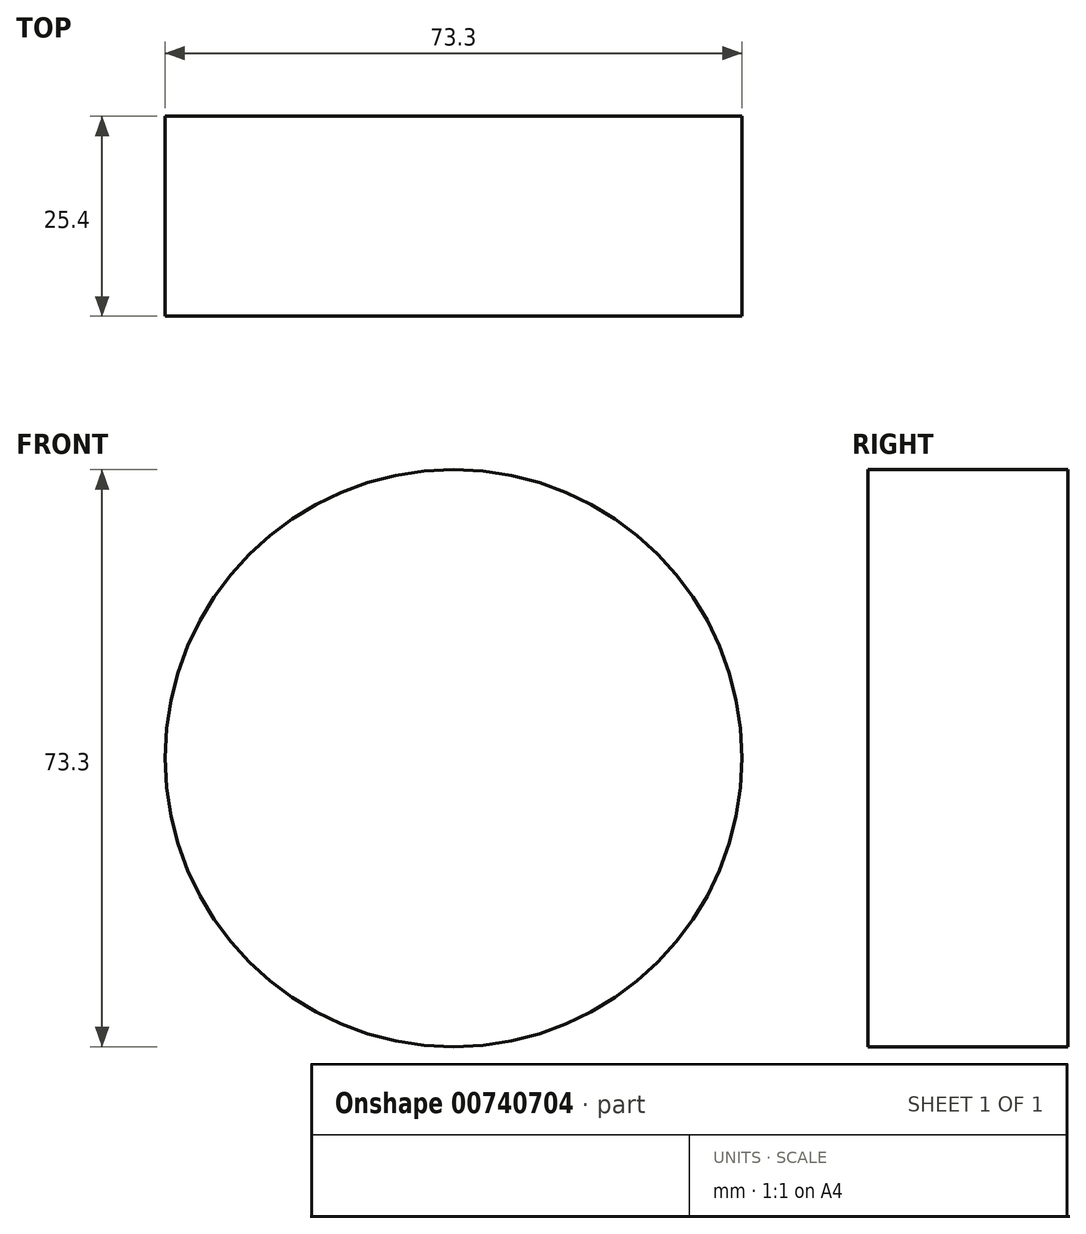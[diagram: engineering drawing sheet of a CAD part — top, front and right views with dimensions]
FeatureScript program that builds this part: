
annotation { "Feature Type Name" : "Feature", "Feature Type Description" : "" }
export const myFeature = defineFeature(function(context is Context, id is Id, definition is map)
    precondition{}
    {
        {
            var Q0;
            Q0=qCreatedBy(makeId("Front.planeOp"),FACE);
            var sketch = newSketch(context, id + "F0", { "sketchPlane" : qUnion([Q0])});
            skCircle(sketch, "E0", {"center": v(0, 0) * mm, "radius": 36.65 * mm});
            skSolve(sketch);
        }
        {
            var Q0;
            Q0=makeQuery(id+"F0.imprint","IMPRINT",FACE,{"disambiguationData":[TD([[makeQuery(id+"F0.imprint","IMPRINT",EDGE,{"derivedFrom":sQuery(id+"F0.wireOp",EDGE,"E0")}),1.0]])]});
            extrude(context, id + "F1", {"entities" : qUnion([Q0]), "depth" : 25.4 * mm, "offsetDistance" : 25.4 * mm});
        }
    });
